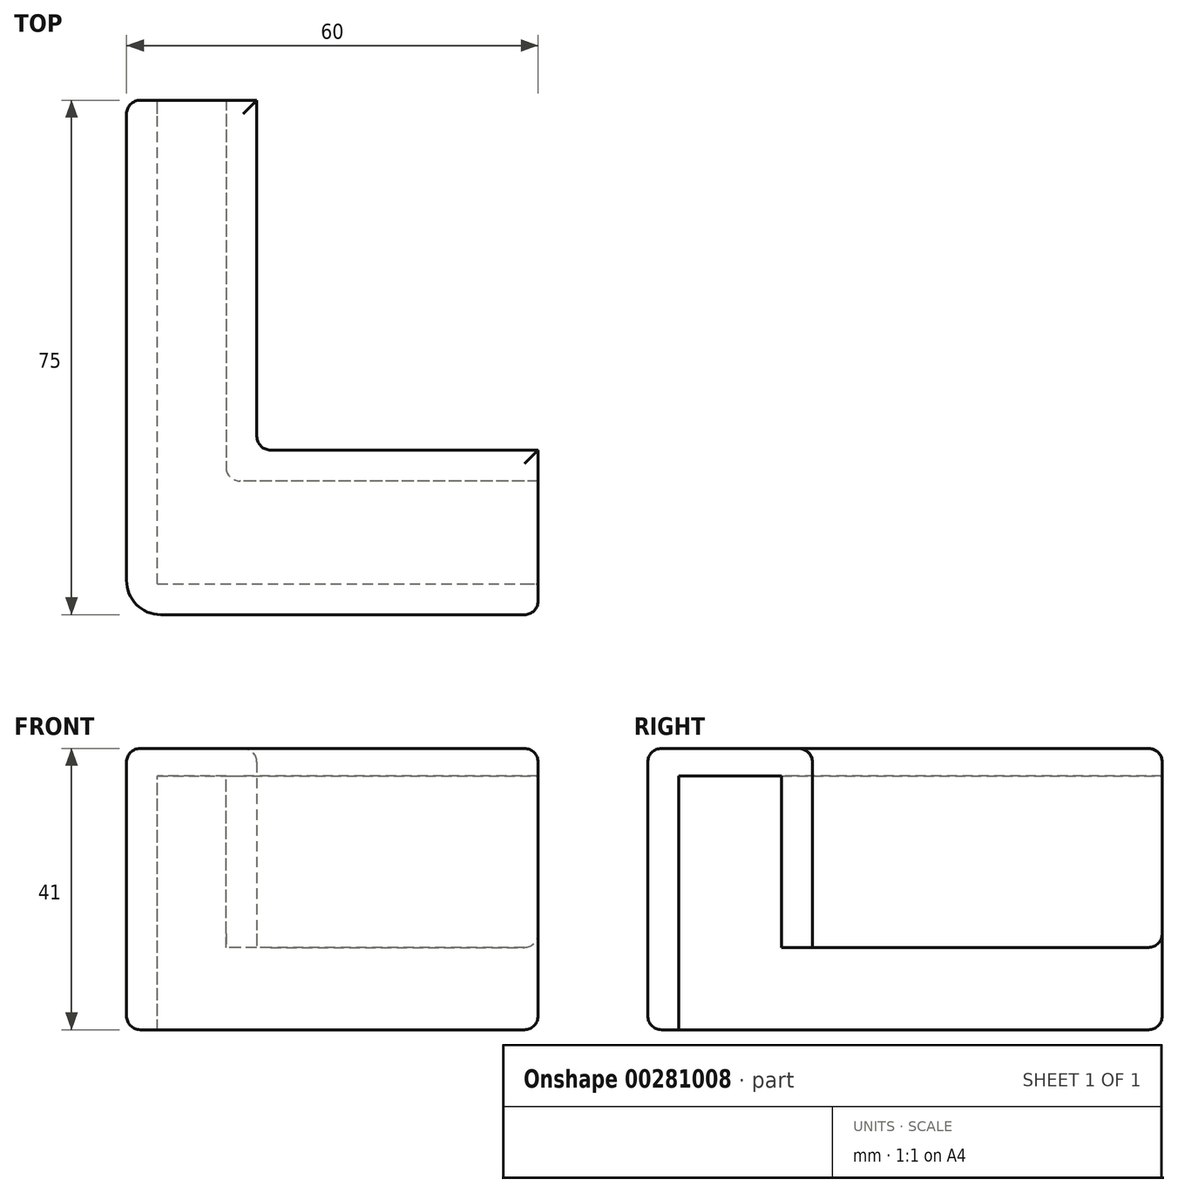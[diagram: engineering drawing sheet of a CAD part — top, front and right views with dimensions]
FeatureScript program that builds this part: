
annotation { "Feature Type Name" : "Feature", "Feature Type Description" : "" }
export const myFeature = defineFeature(function(context is Context, id is Id, definition is map)
    precondition{}
    {
        {
            var Q0;
            Q0=qCreatedBy(makeId("Top.planeOp"),FACE);
            var sketch = newSketch(context, id + "F0", { "sketchPlane" : qUnion([Q0])});
            skLineSegment(sketch, "E0.top", {"start": v(7, 63) * mm, "end": v(-12, 63) * mm});
            skLineSegment(sketch, "E0.left", {"start": v(7, 12) * mm, "end": v(7, 63) * mm});
            skLineSegment(sketch, "E1.bottom", {"start": v(7, 12) * mm, "end": v(48, 12) * mm});
            skLineSegment(sketch, "E1.top", {"start": v(-12, -12) * mm, "end": v(48, -12) * mm});
            skLineSegment(sketch, "E1.right", {"start": v(48, 12) * mm, "end": v(48, -12) * mm});
            skLineSegment(sketch, "E2", {"start": v(-12, -12) * mm, "end": v(-12, 63) * mm});
            skSolve(sketch);
        }
        {
            var Q0;
            Q0 = qSketchRegion(id + "F0", true);
            extrude(context, id + "F1", {"entities" : qUnion([Q0]), "depth" : 4 * mm});
        }
        {
            var Q0;
            Q0=makeQuery(id+"F1.opExtrude","CAP_FACE",FACE,{"disambiguationData":[OSD([sQuery(id+"F0.wireOp",EDGE,"E0.top"),sQuery(id+"F0.wireOp",EDGE,"E0.left"),sQuery(id+"F0.wireOp",EDGE,"E1.bottom"),sQuery(id+"F0.wireOp",EDGE,"E1.top"),sQuery(id+"F0.wireOp",EDGE,"E1.right"),sQuery(id+"F0.wireOp",EDGE,"E2")])],"isStart":true});
            var sketch = newSketch(context, id + "F2", { "sketchPlane" : qUnion([Q0])});
            skLineSegment(sketch, "E3.bottom", {"start": v(-12, 12) * mm, "end": v(48, 12) * mm});
            skLineSegment(sketch, "E3.top", {"start": v(-7.5, 7.5) * mm, "end": v(48, 7.5) * mm});
            skLineSegment(sketch, "E3.right", {"start": v(48, 12) * mm, "end": v(48, 7.5) * mm});
            skLineSegment(sketch, "E4.top", {"start": v(-12, -63) * mm, "end": v(-7.5, -63) * mm});
            skLineSegment(sketch, "E4.right", {"start": v(-7.5, 7.5) * mm, "end": v(-7.5, -63) * mm});
            skLineSegment(sketch, "E5.bottom", {"start": v(7, -63) * mm, "end": v(2.5, -63) * mm});
            skLineSegment(sketch, "E5.left", {"start": v(7, -63) * mm, "end": v(7, -12) * mm});
            skLineSegment(sketch, "E5.right", {"start": v(2.5, -63) * mm, "end": v(2.5, -7.5) * mm});
            skLineSegment(sketch, "E6.bottom", {"start": v(48, -12) * mm, "end": v(7, -12) * mm});
            skLineSegment(sketch, "E6.top", {"start": v(48, -7.5) * mm, "end": v(2.5, -7.5) * mm});
            skLineSegment(sketch, "E6.left", {"start": v(48, -12) * mm, "end": v(48, -7.5) * mm});
            skLineSegment(sketch, "E7", {"start": v(-12, 12) * mm, "end": v(-12, -63) * mm});
            skSolve(sketch);
        }
        {
            var Q0;
            Q0 = qSketchRegion(id + "F2", true);
            extrude(context, id + "F3", {"entities" : qUnion([Q0]), "operationType" : NewBodyOperationType.ADD, "depth" : 25 * mm});
        }
        {
            var Q0;
            Q0=makeQuery(id+"F3.opExtrude","CAP_FACE",FACE,{"disambiguationData":[OSD([sQuery(id+"F2.wireOp",EDGE,"E3.bottom"),sQuery(id+"F2.wireOp",EDGE,"E3.top"),sQuery(id+"F2.wireOp",EDGE,"E3.right"),sQuery(id+"F2.wireOp",EDGE,"E4.top"),sQuery(id+"F2.wireOp",EDGE,"E4.right"),sQuery(id+"F2.wireOp",EDGE,"E7")])],"isStart":false});
            var sketch = newSketch(context, id + "F4", { "sketchPlane" : qUnion([Q0])});
            skLineSegment(sketch, "E8", {"start": v(-12, 12) * mm, "end": v(-12, -63) * mm});
            skLineSegment(sketch, "E9", {"start": v(-12, -63) * mm, "end": v(-7.5, -63) * mm});
            skLineSegment(sketch, "E10", {"start": v(-7.5, -63) * mm, "end": v(-7.5, 7.5) * mm});
            skLineSegment(sketch, "E11", {"start": v(-7.5, 7.5) * mm, "end": v(48, 7.5) * mm});
            skLineSegment(sketch, "E12", {"start": v(48, 7.5) * mm, "end": v(48, 12) * mm});
            skLineSegment(sketch, "E13", {"start": v(48, 12) * mm, "end": v(-12, 12) * mm});
            skSolve(sketch);
        }
        {
            var Q0;
            Q0 = qSketchRegion(id + "F4", true);
            extrude(context, id + "F5", {"entities" : qUnion([Q0]), "operationType" : NewBodyOperationType.ADD, "depth" : 12 * mm});
        }
        {
            var Q0;
            Q0=makeQuery(id+"F1.opExtrude","CAP_FACE",FACE,{"disambiguationData":[OSD([sQuery(id+"F0.wireOp",EDGE,"E0.top"),sQuery(id+"F0.wireOp",EDGE,"E0.left"),sQuery(id+"F0.wireOp",EDGE,"E1.bottom"),sQuery(id+"F0.wireOp",EDGE,"E1.top"),sQuery(id+"F0.wireOp",EDGE,"E1.right"),sQuery(id+"F0.wireOp",EDGE,"E2")])],"isStart":false});
            var Q1;
            Q1=makeQuery(id+"F5.opExtrude","CAP_EDGE",EDGE,{"disambiguationData":[OSD([sQuery(id+"F4.wireOp",EDGE,"E9")])],"isStart":false});
            var Q2;
            Q2=makeQuery(id+"F3.opExtrude","CAP_EDGE",EDGE,{"disambiguationData":[OSD([sQuery(id+"F2.wireOp",EDGE,"E5.bottom")])],"isStart":false});
            var Q3;
            Q3=makeQuery(id+"F5.opExtrude","CAP_EDGE",EDGE,{"disambiguationData":[OSD([sQuery(id+"F4.wireOp",EDGE,"E12")])],"isStart":false});
            var Q4;
            Q4=makeQuery(id+"F3.opExtrude","CAP_EDGE",EDGE,{"disambiguationData":[OSD([sQuery(id+"F2.wireOp",EDGE,"E6.left")])],"isStart":false});
            var Q5;
            Q5=makeQuery(id+"F3.opExtrude","SWEPT_EDGE",EDGE,{"disambiguationData":[OSD([sQuery(id+"F2.wireOp",EDGE,"E5.right"),sQuery(id+"F2.wireOp",EDGE,"E6.top")])]});
            var Q6;
            Q6=makeQuery(id+"F3.boolean.opBoolean","MERGE",EDGE,{"derivedFrom":[makeQuery(id+"F1.opExtrude","SWEPT_EDGE",EDGE,{"disambiguationData":[OSD([sQuery(id+"F0.wireOp",EDGE,"E0.left"),sQuery(id+"F0.wireOp",EDGE,"E1.bottom")])]}),makeQuery(id+"F3.opExtrude","SWEPT_EDGE",EDGE,{"disambiguationData":[OSD([sQuery(id+"F2.wireOp",EDGE,"E5.left"),sQuery(id+"F2.wireOp",EDGE,"E6.bottom")])]})]});
            var Q7;
            Q7=makeQuery(id+"F5.boolean.opBoolean","MERGE",EDGE,{"derivedFrom":[makeQuery(id+"F3.boolean.opBoolean","MERGE",EDGE,{"derivedFrom":[makeQuery(id+"F1.opExtrude","SWEPT_EDGE",EDGE,{"disambiguationData":[OSD([sQuery(id+"F0.wireOp",EDGE,"E0.top"),sQuery(id+"F0.wireOp",EDGE,"E2")])]}),makeQuery(id+"F3.opExtrude","SWEPT_EDGE",EDGE,{"disambiguationData":[OSD([sQuery(id+"F2.wireOp",EDGE,"E4.top"),sQuery(id+"F2.wireOp",EDGE,"E7")])]})]}),makeQuery(id+"F5.opExtrude","SWEPT_EDGE",EDGE,{"disambiguationData":[OSD([sQuery(id+"F4.wireOp",EDGE,"E8"),sQuery(id+"F4.wireOp",EDGE,"E9")])]})]});
            var Q8;
            Q8=makeQuery(id+"F5.boolean.opBoolean","MERGE",EDGE,{"derivedFrom":[makeQuery(id+"F3.boolean.opBoolean","MERGE",EDGE,{"derivedFrom":[makeQuery(id+"F1.opExtrude","SWEPT_EDGE",EDGE,{"disambiguationData":[OSD([sQuery(id+"F0.wireOp",EDGE,"E1.top"),sQuery(id+"F0.wireOp",EDGE,"E1.right")])]}),makeQuery(id+"F3.opExtrude","SWEPT_EDGE",EDGE,{"disambiguationData":[OSD([sQuery(id+"F2.wireOp",EDGE,"E3.bottom"),sQuery(id+"F2.wireOp",EDGE,"E3.right")])]})]}),makeQuery(id+"F5.opExtrude","SWEPT_EDGE",EDGE,{"disambiguationData":[OSD([sQuery(id+"F4.wireOp",EDGE,"E12"),sQuery(id+"F4.wireOp",EDGE,"E13")])]})]});
            var Q9;
            Q9=makeQuery(id+"F5.opExtrude","CAP_EDGE",EDGE,{"disambiguationData":[OSD([sQuery(id+"F4.wireOp",EDGE,"E8")])],"isStart":false});
            var Q10;
            Q10=makeQuery(id+"F5.opExtrude","CAP_EDGE",EDGE,{"disambiguationData":[OSD([sQuery(id+"F4.wireOp",EDGE,"E13")])],"isStart":false});
            fillet(context, id + "F6", {"entities" : qUnion([Q0, Q1, Q2, Q3, Q4, Q5, Q6, Q7, Q8, Q9, Q10]), "radius" : 2 * mm, "tangentPropagation" : true, "allowEdgeOverflow" : false});
        }
        {
            var Q0;
            Q0=makeQuery(id+"F5.boolean.opBoolean","MERGE",EDGE,{"derivedFrom":[makeQuery(id+"F3.boolean.opBoolean","MERGE",EDGE,{"derivedFrom":[makeQuery(id+"F1.opExtrude","SWEPT_EDGE",EDGE,{"disambiguationData":[OSD([sQuery(id+"F0.wireOp",EDGE,"E1.top"),sQuery(id+"F0.wireOp",EDGE,"E2")])]}),makeQuery(id+"F3.opExtrude","SWEPT_EDGE",EDGE,{"disambiguationData":[OSD([sQuery(id+"F2.wireOp",EDGE,"E3.bottom"),sQuery(id+"F2.wireOp",EDGE,"E7")])]})]}),makeQuery(id+"F5.opExtrude","SWEPT_EDGE",EDGE,{"disambiguationData":[OSD([sQuery(id+"F4.wireOp",EDGE,"E8"),sQuery(id+"F4.wireOp",EDGE,"E13")])]})]});
            fillet(context, id + "F7", {"entities" : qUnion([Q0]), "radius" : 5 * mm, "tangentPropagation" : true, "allowEdgeOverflow" : false});
        }
    });
